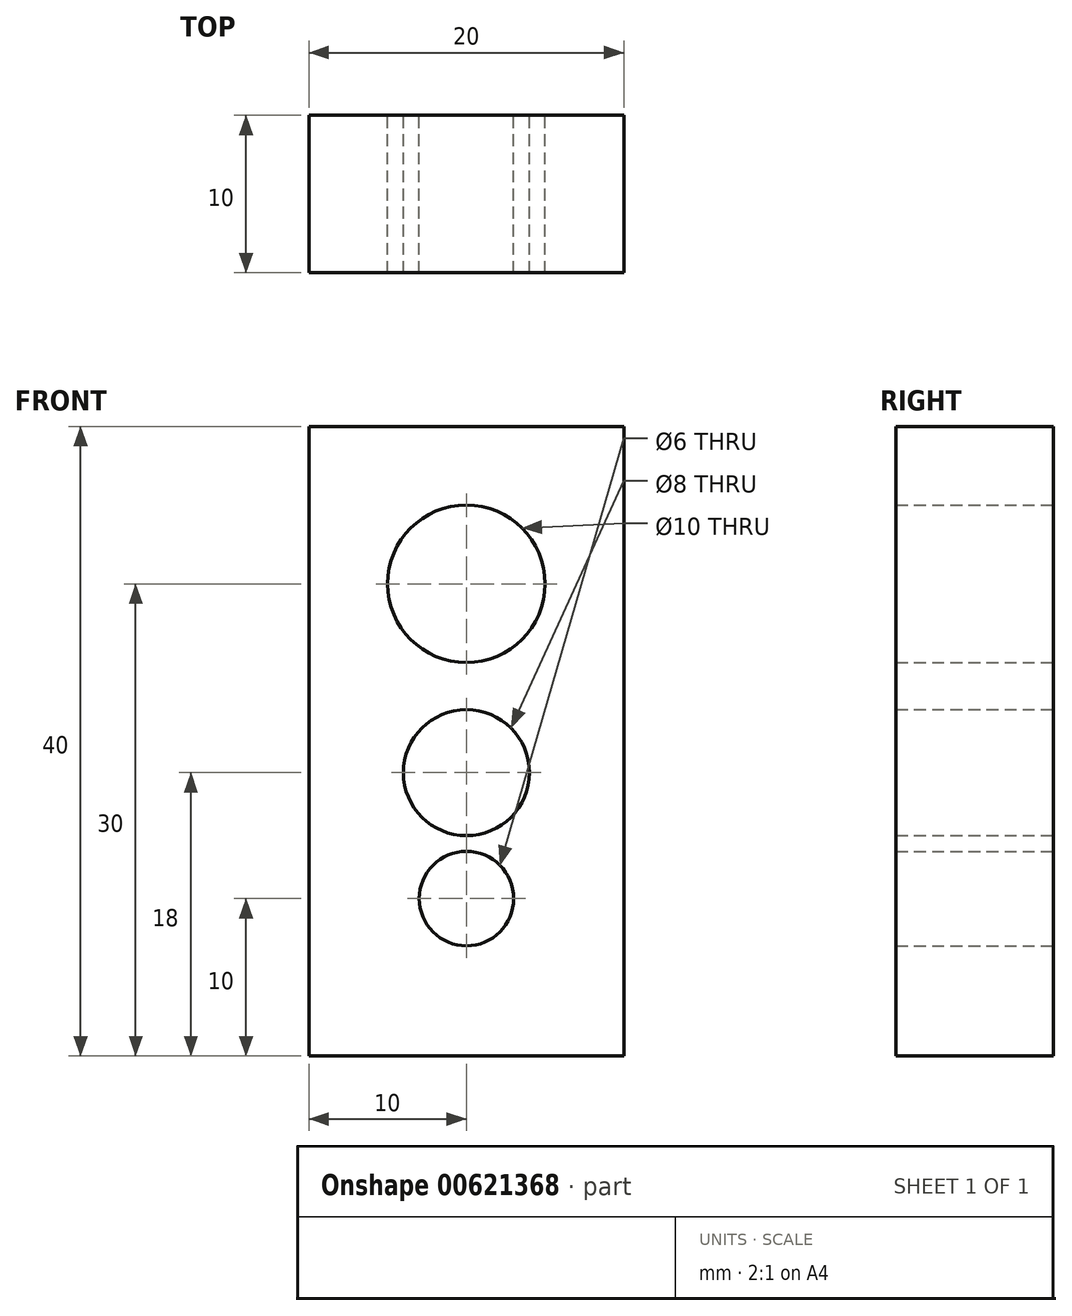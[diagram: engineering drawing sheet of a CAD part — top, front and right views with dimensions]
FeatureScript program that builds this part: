
annotation { "Feature Type Name" : "Feature", "Feature Type Description" : "" }
export const myFeature = defineFeature(function(context is Context, id is Id, definition is map)
    precondition{}
    {
        {
            var Q0;
            Q0=qCreatedBy(makeId("Front.planeOp"),FACE);
            var sketch = newSketch(context, id + "F0", { "sketchPlane" : qUnion([Q0])});
            skLineSegment(sketch, "E0.bottom", {"start": v(-10, 30) * mm, "end": v(10, 30) * mm});
            skLineSegment(sketch, "E0.top", {"start": v(-10, -10) * mm, "end": v(10, -10) * mm});
            skLineSegment(sketch, "E0.left", {"start": v(-10, 30) * mm, "end": v(-10, -10) * mm});
            skLineSegment(sketch, "E0.right", {"start": v(10, 30) * mm, "end": v(10, -10) * mm});
            skCircle(sketch, "E1", {"center": v(0, 0) * mm, "radius": 3 * mm});
            skCircle(sketch, "E2", {"center": v(0, 8) * mm, "radius": 4 * mm});
            skCircle(sketch, "E3", {"center": v(0, 20) * mm, "radius": 5 * mm});
            skSolve(sketch);
        }
        {
            var Q0;
            Q0=makeQuery(id+"F0.imprint","IMPRINT",FACE,{"disambiguationData":[TD([[makeQuery(id+"F0.imprint","IMPRINT",EDGE,{"derivedFrom":sQuery(id+"F0.wireOp",EDGE,"E0.bottom")}),-1.0]])]});
            extrude(context, id + "F1", {"entities" : qUnion([Q0]), "depth" : 10 * mm, "offsetDistance" : 25 * mm});
        }
    });
